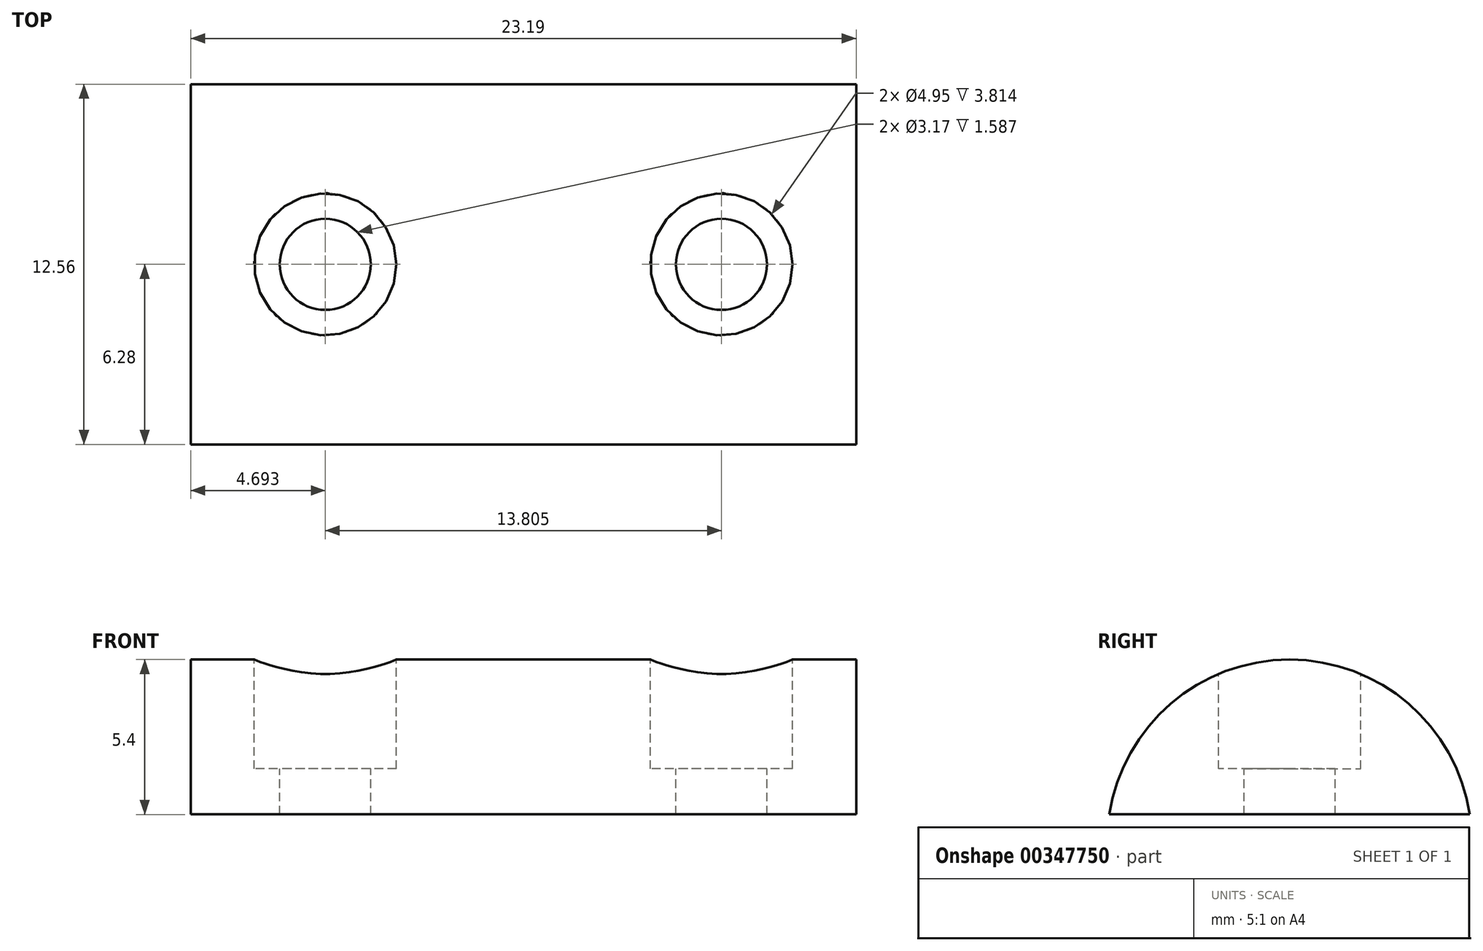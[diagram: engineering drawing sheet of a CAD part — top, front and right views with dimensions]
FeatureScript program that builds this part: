
annotation { "Feature Type Name" : "Feature", "Feature Type Description" : "" }
export const myFeature = defineFeature(function(context is Context, id is Id, definition is map)
    precondition{}
    {
        {
            var Q0;
            Q0=qCreatedBy(makeId("Right.planeOp"),FACE);
            var sketch = newSketch(context, id + "F0", { "sketchPlane" : qUnion([Q0])});
            skCircle(sketch, "E0", {"center": v(0, 0) * mm, "radius": 6.35 * mm});
            skSolve(sketch);
        }
        {
            var Q0;
            Q0 = qSketchRegion(id + "F0", true);
            extrude(context, id + "F1", {"entities" : qUnion([Q0]), "depth" : 23.2 * mm});
        }
        {
            var Q0;
            Q0=makeQuery(id+"F1.opExtrude","CAP_FACE",FACE,{"disambiguationData":[OSD([sQuery(id+"F0.wireOp",EDGE,"E0")])],"isStart":false});
            var sketch = newSketch(context, id + "F2", { "sketchPlane" : qUnion([Q0])});
            skLineSegment(sketch, "E1", {"start": v(-6.28, 0.95) * mm, "end": v(6.28, 0.95) * mm});
            skArc(sketch, "E2.0", {"start": v(-6.28, 0.95) * mm, "mid": v(0, -6.35) * mm, "end": v(6.28, 0.95) * mm});
            skSolve(sketch);
        }
        {
            var Q0;
            Q0 = qSketchRegion(id + "F2", true);
            extrude(context, id + "F3", {"entities" : qUnion([Q0]), "operationType" : NewBodyOperationType.REMOVE, "endBound" : BoundingType.THROUGH_ALL, "oppositeDirection" : true, "depth" : 25.4 * mm});
        }
        {
            var Q0;
            Q0=makeQuery(id+"F3.boolean.opBoolean","COPY",FACE,{"derivedFrom":makeQuery(id+"F3.opExtrude","SWEPT_FACE",FACE,{"disambiguationData":[OSD([sQuery(id+"F2.wireOp",EDGE,"E1")])]})});
            cPlane(context, id + "F4", {"entities" : qUnion([Q0]), "cplaneType" : CPlaneType.OFFSET, "offset" : 5.4 * mm, "oppositeDirection" : true, "width" : 152.4 * mm, "height" : 152.4 * mm});
        }
        {
            var Q0;
            Q0=qCreatedBy(id+"F4.planeOp",FACE);
            var sketch = newSketch(context, id + "F5", { "sketchPlane" : qUnion([Q0])});
            skLineSegment(sketch, "E3.0", {"start": v(0, -6.28) * mm, "end": v(0, 6.28) * mm, "construction": true});
            skLineSegment(sketch, "E4.0", {"start": v(23.2, -6.28) * mm, "end": v(23.2, 6.28) * mm, "construction": true});
            skLineSegment(sketch, "E5", {"start": v(0, 0) * mm, "end": v(23.2, 0) * mm, "construction": true});
            skCircle(sketch, "E6", {"center": v(4.7, 0) * mm, "radius": 2.48 * mm});
            skCircle(sketch, "E7", {"center": v(18.5, 0) * mm, "radius": 2.48 * mm});
            skLineSegment(sketch, "E8", {"start": v(0, -6.28) * mm, "end": v(23.2, -6.28) * mm, "construction": true});
            skLineSegment(sketch, "E9", {"start": v(11.6, -6.28) * mm, "end": v(11.6, 6.28) * mm, "construction": true});
            skSolve(sketch);
        }
        {
            var Q0;
            Q0 = qSketchRegion(id + "F5", true);
            extrude(context, id + "F6", {"entities" : qUnion([Q0]), "operationType" : NewBodyOperationType.REMOVE, "depth" : 3.8 * mm});
        }
        {
            var Q0;
            Q0=makeQuery(id+"F6.boolean.opBoolean","COPY",FACE,{"derivedFrom":makeQuery(id+"F6.opExtrude","CAP_FACE",FACE,{"disambiguationData":[OSD([sQuery(id+"F5.wireOp",EDGE,"E6")])],"isStart":false})});
            var sketch = newSketch(context, id + "F7", { "sketchPlane" : qUnion([Q0])});
            skCircle(sketch, "E10", {"center": v(4.7, 0) * mm, "radius": 1.59 * mm});
            skCircle(sketch, "E11.0", {"center": v(18.5, 0) * mm, "radius": 2.48 * mm, "construction": true});
            skCircle(sketch, "E12", {"center": v(18.5, 0) * mm, "radius": 1.59 * mm});
            skSolve(sketch);
        }
        {
            var Q0;
            Q0 = qSketchRegion(id + "F7", true);
            extrude(context, id + "F8", {"entities" : qUnion([Q0]), "operationType" : NewBodyOperationType.REMOVE, "endBound" : BoundingType.THROUGH_ALL, "oppositeDirection" : true, "depth" : 25.4 * mm});
        }
    });
